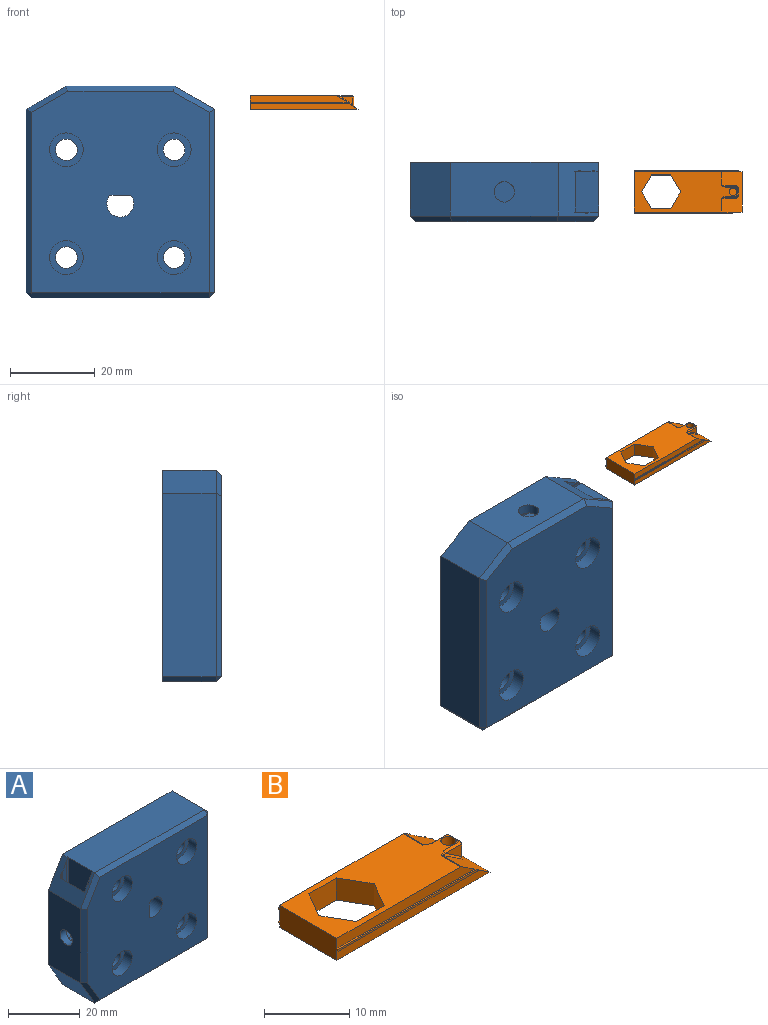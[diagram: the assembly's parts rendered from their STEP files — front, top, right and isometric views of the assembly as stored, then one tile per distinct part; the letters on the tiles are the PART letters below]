
ASSEMBLY  parts=2 mates=2
PART A: 60 faces, bbox 49.9x14x44.5 mm
  f0: plane 3.18x2.27mm, normal (0,0,1), area 6.5mm2, adj f24,f25,f35,f36,f37,f38,f39,f44
  f1: cylinder r=2.41mm len=4.83mm, axis (-1,0,0), area 35.2mm2, adj f9,f25
  f2: cylinder r=2.54mm len=10.8mm, axis (0,1,0), area 172.3mm2, adj f15,f21
  f3: cylinder r=2.54mm len=10.8mm, axis (0,1,0), area 172.3mm2, adj f15,f19
  f4: cylinder r=2.54mm len=10.8mm, axis (0,1,0), area 172.3mm2, adj f15,f17
  f5: cylinder r=2.54mm len=10.8mm, axis (0,1,0), area 172.3mm2, adj f15,f23
  f6: plane 47.41x41.91mm, normal (0,-1,0), area 1718.7mm2, adj f12,f14,f16,f18,f20,f22,f50,f51
  f7: plane 43.18x12.7mm, normal (0,0,1), area 548.4mm2, adj f8,f15,f24,f52,f53
  f8: plane 12.7x9.53mm, normal (-0.87,0,0.5), area 78.8mm2, adj f7,f9,f15,f25,f26,f27,f28,f29
  f9: plane 25.4x12.7mm, normal (-1,0,0), area 304.3mm2, adj f1,f8,f10,f15,f51
  f10: plane 12.7x9.53mm, normal (-0.87,0,-0.5), area 139.7mm2, adj f9,f11,f15,f54
  f11: plane 43.18x12.7mm, normal (0,0,-1), area 548.4mm2, adj f10,f15,f56,f59
  f12: cylinder r=3.17mm len=13.97mm, axis (0,1,0), area 200mm2, adj f6,f14,f15
  f13: plane 41.91x12.7mm, normal (1,0,0), area 532.3mm2, adj f15,f53,f57,f59
  f14: plane 13.97x4.92mm, normal (1,0,0), area 68.7mm2, adj f6,f12,f15
  f15: plane 49.95x44.45mm, normal (0,1,0), area 2057.5mm2, adj f2,f3,f4,f5,f7,f8,f9,f10
  f16: cylinder r=3.97mm len=7.94mm, axis (0,-1,0), area 79.2mm2, adj f6,f17
  f17: plane 7.94x7.94mm, normal (0,-1,0), area 29.2mm2, adj f4,f16
  f18: cylinder r=3.97mm len=7.94mm, axis (0,-1,0), area 79.2mm2, adj f6,f19
  f19: plane 7.94x7.94mm, normal (0,-1,0), area 29.2mm2, adj f3,f18
  f20: cylinder r=3.97mm len=7.94mm, axis (0,-1,0), area 79.2mm2, adj f6,f21
  f21: plane 7.94x7.94mm, normal (0,-1,0), area 29.2mm2, adj f2,f20
  f22: cylinder r=3.97mm len=7.94mm, axis (0,-1,0), area 79.2mm2, adj f6,f23
  f23: plane 7.94x7.94mm, normal (0,-1,0), area 29.2mm2, adj f5,f22
  f24: plane 25.4x9.53mm, normal (-1,0,0), area 191.4mm2, adj f0,f7,f26,f39,f40,f41,f42,f43
  f25: plane 20.69x9.53mm, normal (1,0,0), area 175.3mm2, adj f0,f1,f8,f34,f35,f40,f44,f45
  f26: plane 25.4x0.51mm, normal (0,-1,0), area 12.7mm2, adj f8,f24,f27,f40
  f27: plane 24.52x0.25mm, normal (-1,0,0), area 6.2mm2, adj f8,f26,f28,f40
  f28: plane 24.52x0.25mm, normal (0,-1,0), area 6.2mm2, adj f8,f27,f29,f40
  f29: plane 24.08x0.25mm, normal (1,0,0), area 6.1mm2, adj f8,f28,f30,f40
  f30: plane 24.08x1.65mm, normal (0,-1,0), area 37.4mm2, adj f8,f29,f31,f40
  f31: plane 21.22x0.25mm, normal (-1,0,0), area 5.4mm2, adj f8,f30,f32,f40
  f32: plane 21.22x0.25mm, normal (0,-1,0), area 5.3mm2, adj f8,f31,f33,f40
  f33: plane 20.78x0.25mm, normal (1,0,0), area 5.3mm2, adj f8,f32,f34,f40
  f34: plane 20.78x0.51mm, normal (0,-1,0), area 10.3mm2, adj f8,f25,f33,f40
  f35: plane 22.43x1.46mm, normal (0,1,0), area 30.9mm2, adj f0,f8,f25,f36
  f36: plane 22.43x0.25mm, normal (1,0,0), area 5.7mm2, adj f0,f8,f35,f37
  f37: plane 22.87x0.25mm, normal (0,1,0), area 5.8mm2, adj f0,f8,f36,f38
  f38: plane 22.87x0.25mm, normal (-1,0,0), area 5.8mm2, adj f0,f8,f37,f39
  f39: plane 25.4x1.46mm, normal (0,1,0), area 35.2mm2, adj f0,f8,f24,f38
  f40: plane 3.18x2.27mm, normal (0,0,1), area 6.5mm2, adj f24,f25,f26,f27,f28,f29,f30,f31
  f41: plane 3.97x3.18mm, normal (0,0.87,-0.5), area 14.6mm2, adj f24,f42,f44,f46
  f42: plane 4.58x3.18mm, normal (0,0,-1), area 14.6mm2, adj f24,f41,f43,f46
  f43: plane 3.97x3.18mm, normal (0,-0.87,-0.5), area 14.6mm2, adj f24,f42,f45,f46
  f44: plane 6.35x3.97mm, normal (0,0.87,0.5), area 17.5mm2, adj f0,f24,f25,f41,f46,f47
  f45: plane 6.35x3.97mm, normal (0,-0.87,0.5), area 17.5mm2, adj f24,f25,f40,f43,f46,f47
  f46: plane 9.17x7.94mm, normal (-1,0,0), area 36.3mm2, adj f41,f42,f43,f44,f45,f47,f49
  f47: plane 6.35x4.58mm, normal (0,0,1), area 29.1mm2, adj f25,f44,f45,f46
  f48: plane 4.83x4.83mm, normal (-1,0,0), area 18.3mm2, adj f49
  f49: cylinder r=2.41mm len=15.2mm, axis (-1,0,0), area 230.5mm2, adj f46,f48
  f50: plane 9.87x6.23mm, normal (-0.61,-0.71,0.35), area 18.8mm2, adj f6,f8,f51,f52
  f51: plane 25.4x1.27mm, normal (-0.71,-0.71,0), area 45mm2, adj f6,f9,f50,f54
  f52: plane 43.18x1.27mm, normal (0,-0.71,0.71), area 76.9mm2, adj f6,f7,f50,f55
  f53: plane 12.7x1.27mm, normal (0.71,0,0.71), area 22.8mm2, adj f7,f13,f15,f55
  f54: plane 9.87x6.23mm, normal (-0.61,-0.71,-0.35), area 18.8mm2, adj f6,f10,f51,f56
  f55: plane 1.27x1.27mm, normal (0.58,-0.58,0.58), area 1.4mm2, adj f52,f53,f57
  f56: plane 43.18x1.27mm, normal (0,-0.71,-0.71), area 76.9mm2, adj f6,f11,f54,f58
  f57: plane 41.91x1.27mm, normal (0.71,-0.71,0), area 75.3mm2, adj f6,f13,f55,f58
  f58: plane 1.27x1.27mm, normal (0.58,-0.58,-0.58), area 1.4mm2, adj f56,f57,f59
  f59: plane 12.7x1.27mm, normal (0.71,0,-0.71), area 22.8mm2, adj f11,f13,f15,f58
PART B: 45 faces, bbox 25.6x10.3x3.4 mm
  f0: plane 25.4x0.51mm, normal (0,1,0), area 12.7mm2, adj f3,f4,f8,f21
  f1: plane 24.25x1.65mm, normal (0,1,0), area 38mm2, adj f4,f8,f20,f22
  f2: plane 25.4x1.46mm, normal (0,-1,0), area 35.5mm2, adj f3,f4,f8,f16
  f3: plane 25.4x9.53mm, normal (0,0,-1), area 187.4mm2, adj f0,f2,f4,f8,f9,f10,f11,f12
  f4: plane 10.03x4.72mm, normal (0.55,0,0.83), area 40.5mm2, adj f0,f1,f2,f3,f6,f7,f15,f16
  f5: plane 24.17x9.53mm, normal (0,0,1), area 146.4mm2, adj f6,f7,f8,f9,f10,f11,f12,f13
  f6: plane 22.82x1.46mm, normal (0,-1,0), area 31.7mm2, adj f4,f5,f8,f15,f44
  f7: plane 21.38x0.51mm, normal (0,1,0), area 10.7mm2, adj f4,f5,f8,f18,f29
  f8: plane 10.03x3.18mm, normal (-1,0,0), area 30.4mm2, adj f0,f1,f2,f3,f5,f6,f7,f15
  f9: plane 3.97x3.18mm, normal (0.87,0.5,0), area 14.6mm2, adj f3,f5,f10,f14
  f10: plane 4.58x3.18mm, normal (0,1,0), area 14.6mm2, adj f3,f5,f9,f11
  f11: plane 3.97x3.18mm, normal (-0.87,0.5,0), area 14.6mm2, adj f3,f5,f10,f12
  f12: plane 3.97x3.18mm, normal (-0.87,-0.5,0), area 14.6mm2, adj f3,f5,f11,f13
  f13: plane 4.58x3.18mm, normal (0,-1,0), area 14.6mm2, adj f3,f5,f12,f14
  f14: plane 3.97x3.18mm, normal (0.87,-0.5,0), area 14.6mm2, adj f3,f5,f9,f13
  f15: plane 22.82x0.25mm, normal (0,0,1), area 5.8mm2, adj f4,f6,f8,f17
  f16: plane 23.2x0.25mm, normal (0,0,-1), area 5.9mm2, adj f2,f4,f8,f17
  f17: plane 23.2x0.25mm, normal (0,-1,0), area 5.8mm2, adj f4,f8,f15,f16
  f18: plane 21.38x0.25mm, normal (0,0,1), area 5.4mm2, adj f4,f7,f8,f19
  f19: plane 21.76x0.25mm, normal (0,1,0), area 5.5mm2, adj f4,f8,f18,f20
  f20: plane 21.76x0.25mm, normal (0,0,-1), area 5.5mm2, adj f1,f4,f8,f19
  f21: plane 24.63x0.25mm, normal (0,0,-1), area 6.3mm2, adj f0,f4,f8,f23
  f22: plane 24.25x0.25mm, normal (0,0,1), area 6.2mm2, adj f1,f4,f8,f23
  f23: plane 24.63x0.25mm, normal (0,1,0), area 6.2mm2, adj f4,f8,f21,f22
  f24: plane 2.71x1.8mm, normal (0,1,0), area 2.4mm2, adj f31,f32,f33
  f25: plane 2.71x1.8mm, normal (0,-1,0), area 2.4mm2, adj f37,f41,f42
  f26: plane 2.14x2.03mm, normal (1,0,0), area 4.3mm2, adj f32,f36,f37,f38
  f27: cylinder r=0.89mm len=2.36mm, axis (0,0,1), area 9.9mm2, adj f5,f28
  f28: plane 2.03x2.03mm, normal (0.55,0,0.83), area 3mm2, adj f27
  f29: plane 3.24x0.14mm, normal (0.29,0,0.96), area 0.5mm2, adj f4,f5,f7,f30
  f30: bspline ~0.92x0.51mm, area 0.2mm2, adj f5,f29,f31,f33
  f31: plane 2.71x0.25mm, normal (0,0.71,0.71), area 1mm2, adj f5,f24,f30,f34
  f32: plane 2.14x0.25mm, normal (0.71,0.71,0), area 0.7mm2, adj f24,f26,f34,f35
  f33: plane 3.49x2.22mm, normal (0.39,0.71,0.59), area 1.3mm2, adj f4,f24,f30,f35
  f34: plane 0.25x0.25mm, normal (0.58,0.58,0.58), area 0.1mm2, adj f31,f32,f36
  f35: bspline ~0.55x0.51mm, area 0.2mm2, adj f4,f32,f33,f38
  f36: plane 2.03x0.25mm, normal (0.71,0,0.71), area 0.7mm2, adj f5,f26,f34,f39
  f37: plane 2.14x0.25mm, normal (0.71,-0.71,0), area 0.7mm2, adj f25,f26,f39,f40
  f38: plane 2.03x0.21mm, normal (0.88,0,0.47), area 0.5mm2, adj f4,f26,f35,f40
  f39: plane 0.25x0.25mm, normal (0.58,-0.58,0.58), area 0.1mm2, adj f36,f37,f41
  f40: bspline ~0.55x0.51mm, area 0.2mm2, adj f4,f37,f38,f42
  f41: plane 2.71x0.25mm, normal (0,-0.71,0.71), area 1mm2, adj f5,f25,f39,f43
  f42: plane 3.49x2.22mm, normal (0.39,-0.71,0.59), area 1.3mm2, adj f4,f25,f40,f43
  f43: bspline ~0.92x0.51mm, area 0.2mm2, adj f5,f41,f42,f44
  f44: plane 3.24x0.14mm, normal (0.29,0,0.96), area 0.5mm2, adj f4,f5,f6,f43
PLACE A rot(axis=(0,1,0),90deg) t=(-26.06,0.32,4.59)mm
PLACE B t=(20.43,-1.91,28.4)mm
MATE planar B.f0 <-> A.f26  axis (0,1,0) through (17.06,-1.91,27.07)mm
MATE planar B.f3 <-> A.f24  axis (0,0,-1) through (19.1,-6.67,26.82)mm
